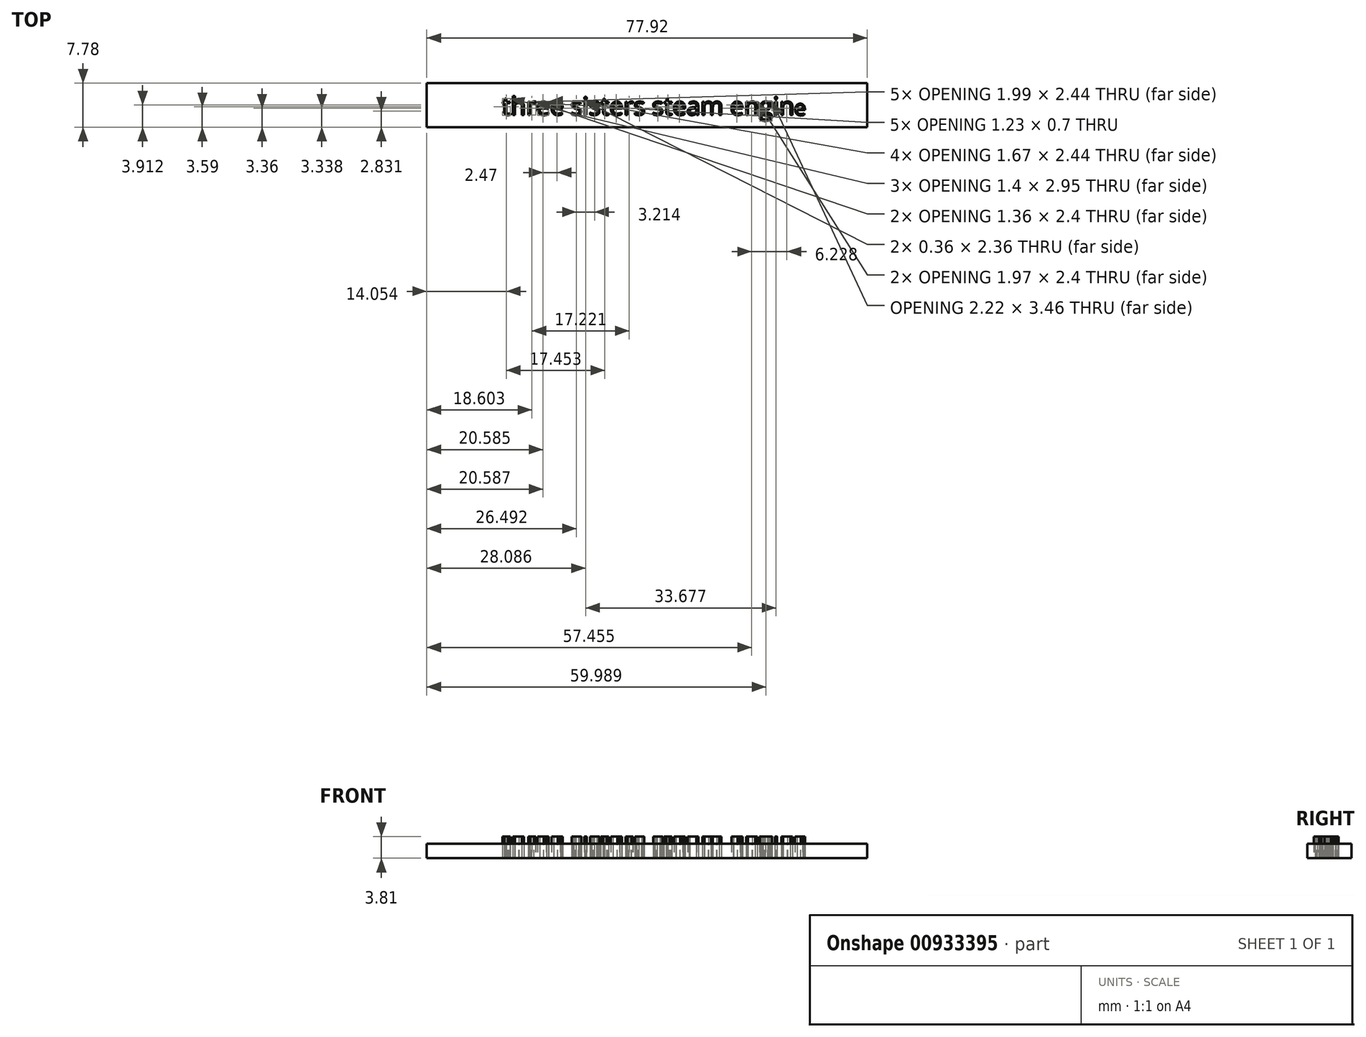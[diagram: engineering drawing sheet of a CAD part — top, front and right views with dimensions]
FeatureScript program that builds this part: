
annotation { "Feature Type Name" : "Feature", "Feature Type Description" : "" }
export const myFeature = defineFeature(function(context is Context, id is Id, definition is map)
    precondition{}
    {
        {
            var Q0;
            Q0=qCreatedBy(makeId("Top.planeOp"),FACE);
            var sketch = newSketch(context, id + "F0", { "sketchPlane" : qUnion([Q0])});
            skLineSegment(sketch, "E0.bottom", {"start": v(-47.03, -21.03) * mm, "end": v(30.9, -21.03) * mm});
            skLineSegment(sketch, "E0.top", {"start": v(-47.03, -13.25) * mm, "end": v(30.9, -13.25) * mm});
            skLineSegment(sketch, "E0.left", {"start": v(-47.03, -21.03) * mm, "end": v(-47.03, -13.25) * mm});
            skLineSegment(sketch, "E0.right", {"start": v(30.9, -21.03) * mm, "end": v(30.9, -13.25) * mm});
            skText(sketch, "E1", { "text": "three sisters steam engin", "fontName": "OpenSans-Regular.ttf"});
            skText(sketch, "E2", { "text": "e", "fontName": "OpenSans-Regular.ttf"});
            const initialGuessF0  = {"E1": [-0.03374, -0.01887, 1, 0, 0.00317], "E2": [0.01792, -0.01893, 1, 0, 0.00274]};
            skSetInitialGuess(sketch, initialGuessF0);
            skSolve(sketch);
        }
        {
            var Q0;
            Q0 = qSketchRegion(id + "F0", true);
            var Q1;
            Q1=makeQuery(id+"F0.imprint","IMPRINT",FACE,{"disambiguationData":[TD([[makeQuery(id+"F0.imprint","IMPRINT",EDGE,{"derivedFrom":sQuery(id+"F0.wireOp",EDGE,"E1.sketch_text.stroke-308")}),1.0]])]});
            var Q2;
            Q2=makeQuery(id+"F0.imprint","IMPRINT",FACE,{"disambiguationData":[TD([[makeQuery(id+"F0.imprint","IMPRINT",EDGE,{"derivedFrom":sQuery(id+"F0.wireOp",EDGE,"E1.sketch_text.stroke-183")}),1.0]])]});
            var Q3;
            Q3=makeQuery(id+"F0.imprint","IMPRINT",FACE,{"disambiguationData":[TD([[makeQuery(id+"F0.imprint","IMPRINT",EDGE,{"derivedFrom":sQuery(id+"F0.wireOp",EDGE,"E1.sketch_text.stroke-83")}),1.0]])]});
            var Q4;
            Q4=makeQuery(id+"F0.imprint","IMPRINT",FACE,{"disambiguationData":[TD([[makeQuery(id+"F0.imprint","IMPRINT",EDGE,{"derivedFrom":sQuery(id+"F0.wireOp",EDGE,"E1.sketch_text.stroke-64")}),1.0]])]});
            var Q5;
            Q5=makeQuery(id+"F0.imprint","IMPRINT",FACE,{"disambiguationData":[TD([[makeQuery(id+"F0.imprint","IMPRINT",EDGE,{"derivedFrom":sQuery(id+"F0.wireOp",EDGE,"E1.sketch_text.stroke-418")}),1.0]])]});
            var Q6;
            Q6=makeQuery(id+"F0.imprint","IMPRINT",FACE,{"disambiguationData":[TD([[makeQuery(id+"F0.imprint","IMPRINT",EDGE,{"derivedFrom":sQuery(id+"F0.wireOp",EDGE,"E1.sketch_text.stroke-409")}),1.0]])]});
            var Q7;
            Q7=makeQuery(id+"F0.imprint","IMPRINT",FACE,{"disambiguationData":[TD([[makeQuery(id+"F0.imprint","IMPRINT",EDGE,{"derivedFrom":sQuery(id+"F0.wireOp",EDGE,"E1.sketch_text.stroke-358")}),1.0]])]});
            var Q8;
            Q8=makeQuery(id+"F0.imprint","IMPRINT",FACE,{"disambiguationData":[TD([[makeQuery(id+"F0.imprint","IMPRINT",EDGE,{"derivedFrom":sQuery(id+"F0.wireOp",EDGE,"E1.sketch_text.stroke-284")}),1.0]])]});
            var Q9;
            Q9=makeQuery(id+"F0.imprint","IMPRINT",FACE,{"disambiguationData":[TD([[makeQuery(id+"F0.imprint","IMPRINT",EDGE,{"derivedFrom":sQuery(id+"F0.wireOp",EDGE,"E2.sketch_text.stroke-14")}),1.0]])]});
            extrude(context, id + "F1", {"entities" : qUnion([Q0, Q1, Q2, Q3, Q4, Q5, Q6, Q7, Q8, Q9]), "depth" : 2.54 * mm, "offsetDistance" : 25.4 * mm});
        }
        {
            var Q0;
            Q0=makeQuery(id+"F0.imprint","IMPRINT",FACE,{"disambiguationData":[TD([[makeQuery(id+"F0.imprint","IMPRINT",EDGE,{"derivedFrom":sQuery(id+"F0.wireOp",EDGE,"E1.sketch_text.stroke-0")}),-1.0]])]});
            var Q1;
            Q1=makeQuery(id+"F0.imprint","IMPRINT",FACE,{"disambiguationData":[TD([[makeQuery(id+"F0.imprint","IMPRINT",EDGE,{"derivedFrom":sQuery(id+"F0.wireOp",EDGE,"E1.sketch_text.stroke-19")}),-1.0]])]});
            var Q2;
            Q2=makeQuery(id+"F0.imprint","IMPRINT",FACE,{"disambiguationData":[TD([[makeQuery(id+"F0.imprint","IMPRINT",EDGE,{"derivedFrom":sQuery(id+"F0.wireOp",EDGE,"E1.sketch_text.stroke-37")}),-1.0]])]});
            var Q3;
            Q3=makeQuery(id+"F0.imprint","IMPRINT",FACE,{"disambiguationData":[TD([[makeQuery(id+"F0.imprint","IMPRINT",EDGE,{"derivedFrom":sQuery(id+"F0.wireOp",EDGE,"E1.sketch_text.stroke-50")}),-1.0]])]});
            var Q4;
            Q4=makeQuery(id+"F0.imprint","IMPRINT",FACE,{"disambiguationData":[TD([[makeQuery(id+"F0.imprint","IMPRINT",EDGE,{"derivedFrom":sQuery(id+"F0.wireOp",EDGE,"E1.sketch_text.stroke-69")}),-1.0]])]});
            var Q5;
            Q5=makeQuery(id+"F0.imprint","IMPRINT",FACE,{"disambiguationData":[TD([[makeQuery(id+"F0.imprint","IMPRINT",EDGE,{"derivedFrom":sQuery(id+"F0.wireOp",EDGE,"E1.sketch_text.stroke-88")}),-1.0]])]});
            var Q6;
            Q6=makeQuery(id+"F0.imprint","IMPRINT",FACE,{"disambiguationData":[TD([[makeQuery(id+"F0.imprint","IMPRINT",EDGE,{"derivedFrom":sQuery(id+"F0.wireOp",EDGE,"E1.sketch_text.stroke-113")}),-1.0]])]});
            var Q7;
            Q7=makeQuery(id+"F0.imprint","IMPRINT",FACE,{"disambiguationData":[TD([[makeQuery(id+"F0.imprint","IMPRINT",EDGE,{"derivedFrom":sQuery(id+"F0.wireOp",EDGE,"E1.sketch_text.stroke-117")}),-1.0]])]});
            var Q8;
            Q8=makeQuery(id+"F0.imprint","IMPRINT",FACE,{"disambiguationData":[TD([[makeQuery(id+"F0.imprint","IMPRINT",EDGE,{"derivedFrom":sQuery(id+"F0.wireOp",EDGE,"E1.sketch_text.stroke-125")}),-1.0]])]});
            var Q9;
            Q9=makeQuery(id+"F0.imprint","IMPRINT",FACE,{"disambiguationData":[TD([[makeQuery(id+"F0.imprint","IMPRINT",EDGE,{"derivedFrom":sQuery(id+"F0.wireOp",EDGE,"E1.sketch_text.stroke-150")}),-1.0]])]});
            var Q10;
            Q10=makeQuery(id+"F0.imprint","IMPRINT",FACE,{"disambiguationData":[TD([[makeQuery(id+"F0.imprint","IMPRINT",EDGE,{"derivedFrom":sQuery(id+"F0.wireOp",EDGE,"E1.sketch_text.stroke-169")}),-1.0]])]});
            var Q11;
            Q11=makeQuery(id+"F0.imprint","IMPRINT",FACE,{"disambiguationData":[TD([[makeQuery(id+"F0.imprint","IMPRINT",EDGE,{"derivedFrom":sQuery(id+"F0.wireOp",EDGE,"E1.sketch_text.stroke-188")}),-1.0]])]});
            var Q12;
            Q12=makeQuery(id+"F0.imprint","IMPRINT",FACE,{"disambiguationData":[TD([[makeQuery(id+"F0.imprint","IMPRINT",EDGE,{"derivedFrom":sQuery(id+"F0.wireOp",EDGE,"E1.sketch_text.stroke-201")}),-1.0]])]});
            var Q13;
            Q13=makeQuery(id+"F0.imprint","IMPRINT",FACE,{"disambiguationData":[TD([[makeQuery(id+"F0.imprint","IMPRINT",EDGE,{"derivedFrom":sQuery(id+"F0.wireOp",EDGE,"E1.sketch_text.stroke-226")}),-1.0]])]});
            var Q14;
            Q14=makeQuery(id+"F0.imprint","IMPRINT",FACE,{"disambiguationData":[TD([[makeQuery(id+"F0.imprint","IMPRINT",EDGE,{"derivedFrom":sQuery(id+"F0.wireOp",EDGE,"E1.sketch_text.stroke-251")}),-1.0]])]});
            var Q15;
            Q15=makeQuery(id+"F0.imprint","IMPRINT",FACE,{"disambiguationData":[TD([[makeQuery(id+"F0.imprint","IMPRINT",EDGE,{"derivedFrom":sQuery(id+"F0.wireOp",EDGE,"E1.sketch_text.stroke-270")}),-1.0]])]});
            var Q16;
            Q16=makeQuery(id+"F0.imprint","IMPRINT",FACE,{"disambiguationData":[TD([[makeQuery(id+"F0.imprint","IMPRINT",EDGE,{"derivedFrom":sQuery(id+"F0.wireOp",EDGE,"E1.sketch_text.stroke-289")}),-1.0]])]});
            var Q17;
            Q17=makeQuery(id+"F0.imprint","IMPRINT",FACE,{"disambiguationData":[TD([[makeQuery(id+"F0.imprint","IMPRINT",EDGE,{"derivedFrom":sQuery(id+"F0.wireOp",EDGE,"E1.sketch_text.stroke-316")}),-1.0]])]});
            var Q18;
            Q18=makeQuery(id+"F0.imprint","IMPRINT",FACE,{"disambiguationData":[TD([[makeQuery(id+"F0.imprint","IMPRINT",EDGE,{"derivedFrom":sQuery(id+"F0.wireOp",EDGE,"E1.sketch_text.stroke-344")}),-1.0]])]});
            var Q19;
            Q19=makeQuery(id+"F0.imprint","IMPRINT",FACE,{"disambiguationData":[TD([[makeQuery(id+"F0.imprint","IMPRINT",EDGE,{"derivedFrom":sQuery(id+"F0.wireOp",EDGE,"E1.sketch_text.stroke-363")}),-1.0]])]});
            var Q20;
            Q20=makeQuery(id+"F0.imprint","IMPRINT",FACE,{"disambiguationData":[TD([[makeQuery(id+"F0.imprint","IMPRINT",EDGE,{"derivedFrom":sQuery(id+"F0.wireOp",EDGE,"E1.sketch_text.stroke-380")}),-1.0]])]});
            var Q21;
            Q21=makeQuery(id+"F0.imprint","IMPRINT",FACE,{"disambiguationData":[TD([[makeQuery(id+"F0.imprint","IMPRINT",EDGE,{"derivedFrom":sQuery(id+"F0.wireOp",EDGE,"E1.sketch_text.stroke-424")}),-1.0]])]});
            var Q22;
            Q22=makeQuery(id+"F0.imprint","IMPRINT",FACE,{"disambiguationData":[TD([[makeQuery(id+"F0.imprint","IMPRINT",EDGE,{"derivedFrom":sQuery(id+"F0.wireOp",EDGE,"E1.sketch_text.stroke-428")}),-1.0]])]});
            var Q23;
            Q23=makeQuery(id+"F0.imprint","IMPRINT",FACE,{"disambiguationData":[TD([[makeQuery(id+"F0.imprint","IMPRINT",EDGE,{"derivedFrom":sQuery(id+"F0.wireOp",EDGE,"E1.sketch_text.stroke-436")}),-1.0]])]});
            var Q24;
            Q24=makeQuery(id+"F0.imprint","IMPRINT",FACE,{"disambiguationData":[TD([[makeQuery(id+"F0.imprint","IMPRINT",EDGE,{"derivedFrom":sQuery(id+"F0.wireOp",EDGE,"E2.sketch_text.stroke-0")}),-1.0]])]});
            extrude(context, id + "F2", {"entities" : qUnion([Q0, Q1, Q2, Q3, Q4, Q5, Q6, Q7, Q8, Q9, Q10, Q11, Q12, Q13, Q14, Q15, Q16, Q17, Q18, Q19, Q20, Q21, Q22, Q23, Q24]), "depth" : 3.8 * mm, "offsetDistance" : 25.4 * mm});
        }
    });
